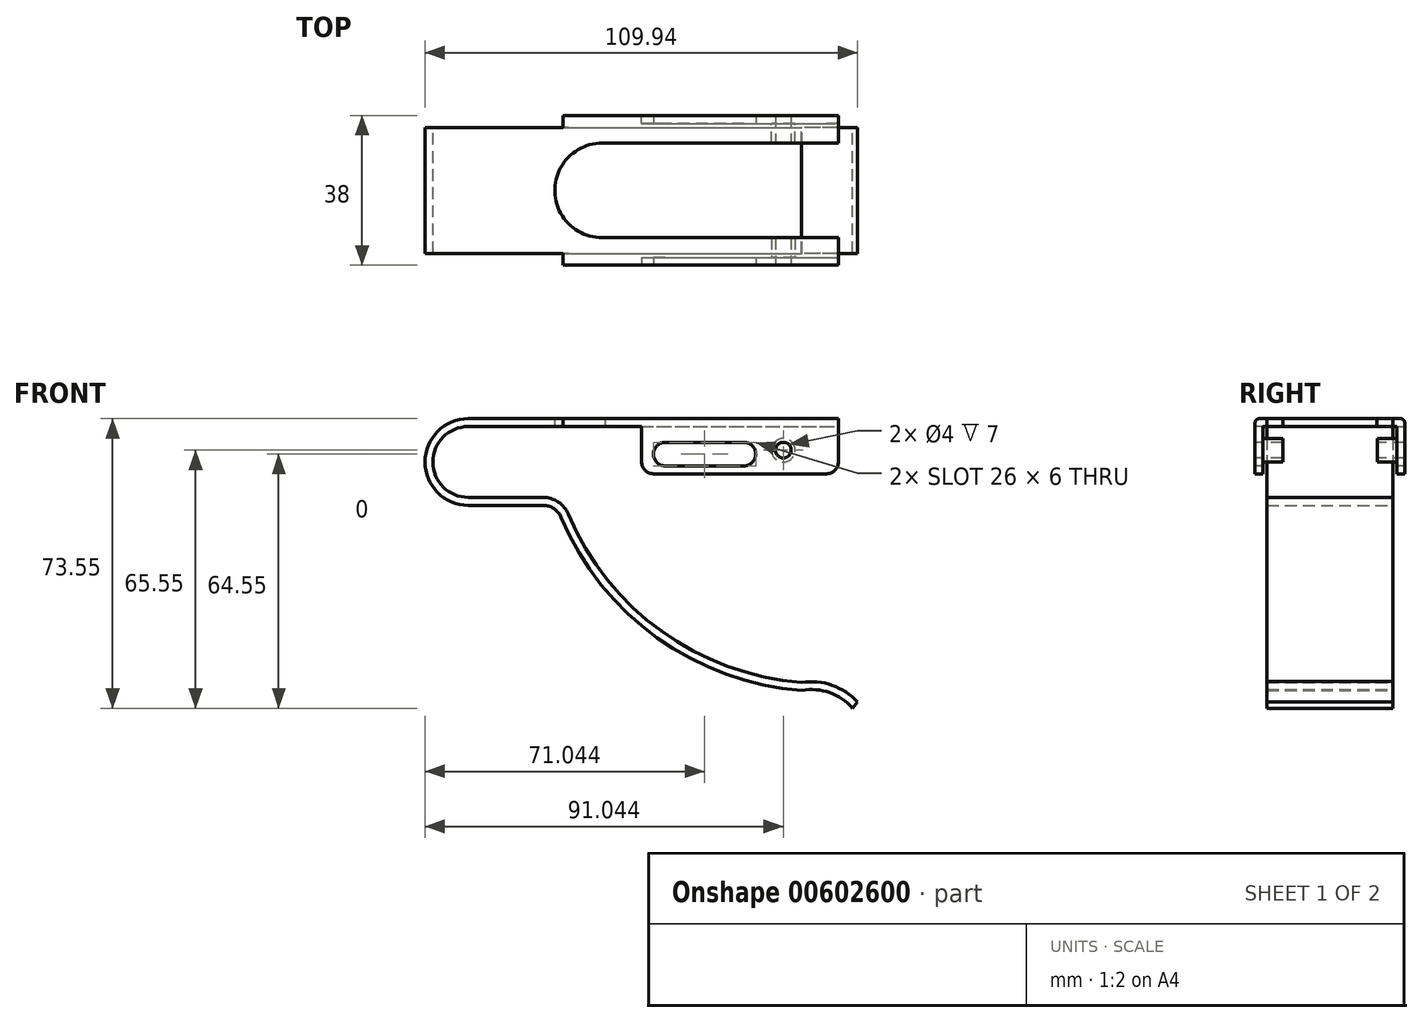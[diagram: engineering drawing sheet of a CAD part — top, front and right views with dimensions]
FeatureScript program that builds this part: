
annotation { "Feature Type Name" : "Feature", "Feature Type Description" : "" }
export const myFeature = defineFeature(function(context is Context, id is Id, definition is map)
    precondition{}
    {
        {
            var Q0;
            Q0=qCreatedBy(makeId("Front.planeOp"),FACE);
            var sketch = newSketch(context, id + "F0", { "sketchPlane" : qUnion([Q0])});
            skArc(sketch, "E0", {"start": v(0, 11) * mm, "mid": v(-11, 0) * mm, "end": v(0, -11) * mm});
            skLineSegment(sketch, "E1", {"start": v(0, 11) * mm, "end": v(94, 11) * mm});
            skLineSegment(sketch, "E2", {"start": v(0, -11) * mm, "end": v(19, -11) * mm});
            skArc(sketch, "E3", {"start": v(23.61, -14.06) * mm, "mid": v(48, -44.68) * mm, "end": v(84.8, -58.01) * mm});
            skArc(sketch, "E4", {"start": v(97.64, -62.55) * mm, "mid": v(91.8, -58.6) * mm, "end": v(84.8, -58.01) * mm});
            skPoint(sketch, "E5.visualSharp", {"position": v(22.4, -11) * mm});
            skArc(sketch, "E5.filletArc", {"start": v(23.61, -14.06) * mm, "mid": v(21.77, -11.84) * mm, "end": v(19, -11) * mm});
            skLineSegment(sketch, "E6.0", {"start": v(0, 9) * mm, "end": v(94, 9) * mm});
            skArc(sketch, "E6.1", {"start": v(0, 9) * mm, "mid": v(-9, 0) * mm, "end": v(0, -9) * mm});
            skArc(sketch, "E6.2", {"start": v(98.94, -61) * mm, "mid": v(92.45, -56.72) * mm, "end": v(84.7, -56) * mm});
            skArc(sketch, "E6.3", {"start": v(25.45, -13.3) * mm, "mid": v(49.07, -42.99) * mm, "end": v(84.7, -56) * mm});
            skArc(sketch, "E6.4", {"start": v(25.45, -13.3) * mm, "mid": v(22.88, -10.17) * mm, "end": v(19, -9) * mm});
            skLineSegment(sketch, "E6.5", {"start": v(0, -9) * mm, "end": v(19, -9) * mm});
            skLineSegment(sketch, "E7", {"start": v(97.64, -62.55) * mm, "end": v(98.94, -61) * mm});
            skLineSegment(sketch, "E8", {"start": v(94, 11) * mm, "end": v(94, 9) * mm});
            skSolve(sketch);
        }
        {
            var Q0;
            Q0 = qSketchRegion(id + "F0", true);
            extrude(context, id + "F1", {"entities" : qUnion([Q0]), "depth" : 16 * mm, "offsetDistance" : 25 * mm});
        }
        {
            var Q0;
            Q0=makeQuery(id+"F1.opExtrude","SWEPT_FACE",FACE,{"disambiguationData":[OSD([sQuery(id+"F0.wireOp",EDGE,"E1")])]});
            var sketch = newSketch(context, id + "F2", { "sketchPlane" : qUnion([Q0])});
            skLineSegment(sketch, "E9.bottom", {"start": v(24.04, -16) * mm, "end": v(94.04, -16) * mm});
            skLineSegment(sketch, "E9.top", {"start": v(24.04, -19) * mm, "end": v(94.04, -19) * mm});
            skLineSegment(sketch, "E9.left", {"start": v(24.04, -16) * mm, "end": v(24.04, -19) * mm});
            skLineSegment(sketch, "E9.right", {"start": v(94.04, -16) * mm, "end": v(94.04, -19) * mm});
            skSolve(sketch);
        }
        {
            var Q0;
            Q0 = qSketchRegion(id + "F2", true);
            extrude(context, id + "F3", {"entities" : qUnion([Q0]), "operationType" : NewBodyOperationType.ADD, "oppositeDirection" : true, "depth" : 2 * mm, "offsetDistance" : 25 * mm});
        }
        {
            var Q0;
            Q0=makeQuery(id+"F3.opExtrude","SWEPT_FACE",FACE,{"disambiguationData":[OSD([sQuery(id+"F2.wireOp",EDGE,"E9.top")])]});
            var sketch = newSketch(context, id + "F4", { "sketchPlane" : qUnion([Q0])});
            skLineSegment(sketch, "E10.bottom", {"start": v(44.04, 11) * mm, "end": v(94.04, 11) * mm});
            skLineSegment(sketch, "E10.top", {"start": v(44.04, -3) * mm, "end": v(94.04, -3) * mm});
            skLineSegment(sketch, "E10.left", {"start": v(44.04, 11) * mm, "end": v(44.04, -3) * mm});
            skLineSegment(sketch, "E10.right", {"start": v(94.04, 11) * mm, "end": v(94.04, -3) * mm});
            skSolve(sketch);
        }
        {
            var Q0;
            Q0 = qSketchRegion(id + "F4", true);
            extrude(context, id + "F5", {"entities" : qUnion([Q0]), "operationType" : NewBodyOperationType.ADD, "oppositeDirection" : true, "depth" : 2 * mm, "offsetDistance" : 25 * mm});
        }
        {
            var Q0;
            Q0=makeQuery(id+"F3.opExtrude","CAP_EDGE",EDGE,{"disambiguationData":[OSD([sQuery(id+"F2.wireOp",EDGE,"E9.top")])],"isStart":true});
            fillet(context, id + "F6", {"entities" : qUnion([Q0]), "radius" : 1 * mm, "tangentPropagation" : true, "allowEdgeOverflow" : false});
        }
        {
            var Q0;
            Q0=makeQuery(id+"F1.opExtrude","SWEPT_BODY",BODY,{"disambiguationData":[OSD([sQuery(id+"F0.wireOp",EDGE,"E0"),sQuery(id+"F0.wireOp",EDGE,"E1"),sQuery(id+"F0.wireOp",EDGE,"E2"),sQuery(id+"F0.wireOp",EDGE,"E3"),sQuery(id+"F0.wireOp",EDGE,"E4"),sQuery(id+"F0.wireOp",EDGE,"E5.filletArc"),sQuery(id+"F0.wireOp",EDGE,"E6.0"),sQuery(id+"F0.wireOp",EDGE,"E6.1"),sQuery(id+"F0.wireOp",EDGE,"E6.2"),sQuery(id+"F0.wireOp",EDGE,"E6.3"),sQuery(id+"F0.wireOp",EDGE,"E6.4"),sQuery(id+"F0.wireOp",EDGE,"E6.5"),sQuery(id+"F0.wireOp",EDGE,"E7"),sQuery(id+"F0.wireOp",EDGE,"E8")])]});
            var Q1;
            Q1=qCreatedBy(makeId("Front.planeOp"),FACE);
            mirror(context, id + "F7", {"operationType" : NewBodyOperationType.ADD, "entities" : qUnion([Q0]), "mirrorPlane" : qUnion([Q1])});
        }
        {
            var Q0;
            {var subQ0=makeQuery(id+"F3.boolean.opBoolean","MERGE",FACE,{"derivedFrom":[makeQuery(id+"F1.opExtrude","SWEPT_FACE",FACE,{"disambiguationData":[OSD([sQuery(id+"F0.wireOp",EDGE,"E1")])]}),makeQuery(id+"F3.opExtrude","CAP_FACE",FACE,{"disambiguationData":[OSD([sQuery(id+"F2.wireOp",EDGE,"E9.bottom"),sQuery(id+"F2.wireOp",EDGE,"E9.top"),sQuery(id+"F2.wireOp",EDGE,"E9.left"),sQuery(id+"F2.wireOp",EDGE,"E9.right")])],"isStart":true})]});Q0=makeQuery(id+"F7.boolean.opBoolean","MERGE",FACE,{"derivedFrom":[subQ0,makeQuery(id+"F7.opPattern","COPY",FACE,{"derivedFrom":subQ0,"instanceName":"1"})]});}
            var sketch = newSketch(context, id + "F8", { "sketchPlane" : qUnion([Q0])});
            skArc(sketch, "E11", {"start": v(34.87, 11.97) * mm, "mid": v(22, 0.4) * mm, "end": v(34.08, -12) * mm});
            skLineSegment(sketch, "E12", {"start": v(34.08, -12) * mm, "end": v(94, -12) * mm});
            skLineSegment(sketch, "E13", {"start": v(33.13, 11.97) * mm, "end": v(94, 11.97) * mm});
            skLineSegment(sketch, "E14", {"start": v(94, 11.97) * mm, "end": v(94, -12) * mm});
            skSolve(sketch);
        }
        {
            var Q0;
            Q0 = qSketchRegion(id + "F8", true);
            extrude(context, id + "F9", {"entities" : qUnion([Q0]), "operationType" : NewBodyOperationType.REMOVE, "oppositeDirection" : true, "depth" : 2 * mm, "offsetDistance" : 25 * mm});
        }
        {
            var Q0;
            Q0=makeQuery(id+"F5.boolean.opBoolean","MERGE",FACE,{"derivedFrom":[makeQuery(id+"F3.opExtrude","SWEPT_FACE",FACE,{"disambiguationData":[OSD([sQuery(id+"F2.wireOp",EDGE,"E9.top")])]}),makeQuery(id+"F5.opExtrude","CAP_FACE",FACE,{"disambiguationData":[OSD([sQuery(id+"F4.wireOp",EDGE,"E10.bottom"),sQuery(id+"F4.wireOp",EDGE,"E10.top"),sQuery(id+"F4.wireOp",EDGE,"E10.left"),sQuery(id+"F4.wireOp",EDGE,"E10.right")])],"isStart":true})]});
            var sketch = newSketch(context, id + "F10", { "sketchPlane" : qUnion([Q0])});
            skLineSegment(sketch, "E15", {"start": v(50.04, 2) * mm, "end": v(70.04, 2) * mm});
            skArc(sketch, "E16.0.startCap", {"start": v(50.04, -1) * mm, "mid": v(47.04, 2) * mm, "end": v(50.04, 5) * mm});
            skArc(sketch, "E16.0.endCap", {"start": v(70.04, 5) * mm, "mid": v(73.04, 2) * mm, "end": v(70.04, -1) * mm});
            skLineSegment(sketch, "E16.0.left", {"start": v(50.04, 5) * mm, "end": v(70.04, 5) * mm});
            skLineSegment(sketch, "E16.0.right", {"start": v(50.04, -1) * mm, "end": v(70.04, -1) * mm});
            skPoint(sketch, "E17", {"position": v(80.04, 3) * mm});
            skSolve(sketch);
        }
        {
            var Q0;
            Q0 = qSketchRegion(id + "F10", true);
            extrude(context, id + "F11", {"entities" : qUnion([Q0]), "operationType" : NewBodyOperationType.REMOVE, "endBound" : BoundingType.THROUGH_ALL, "oppositeDirection" : true, "depth" : 25 * mm, "offsetDistance" : 25 * mm});
        }
        {
            var Q0;
            Q0=sQuery(id+"F10.wireOp",VERTEX,"E17");
            var Q1;
            Q1=makeQuery(id+"F1.opExtrude","SWEPT_BODY",BODY,{"disambiguationData":[OSD([sQuery(id+"F0.wireOp",EDGE,"E0"),sQuery(id+"F0.wireOp",EDGE,"E1"),sQuery(id+"F0.wireOp",EDGE,"E2"),sQuery(id+"F0.wireOp",EDGE,"E3"),sQuery(id+"F0.wireOp",EDGE,"E4"),sQuery(id+"F0.wireOp",EDGE,"E5.filletArc"),sQuery(id+"F0.wireOp",EDGE,"E6.0"),sQuery(id+"F0.wireOp",EDGE,"E6.1"),sQuery(id+"F0.wireOp",EDGE,"E6.2"),sQuery(id+"F0.wireOp",EDGE,"E6.3"),sQuery(id+"F0.wireOp",EDGE,"E6.4"),sQuery(id+"F0.wireOp",EDGE,"E6.5"),sQuery(id+"F0.wireOp",EDGE,"E7"),sQuery(id+"F0.wireOp",EDGE,"E8")])]});
            hole(context, id + "F12", {"style" : HoleStyle.SIMPLE, "endStyle" : HoleEndStyle.THROUGH, "holeDiameter" : 4 * mm, "majorDiameter" : 5 * mm, "isTappedThrough" : true, "tappedDepth" : 12 * mm, "tapClearance" : 3, "locations" : qUnion([Q0]), "scope" : qUnion([Q1])});
        }
        {
            var Q0;
            Q0=makeQuery(id+"F5.opExtrude","CAP_FACE",FACE,{"disambiguationData":[OSD([sQuery(id+"F4.wireOp",EDGE,"E10.bottom"),sQuery(id+"F4.wireOp",EDGE,"E10.top"),sQuery(id+"F4.wireOp",EDGE,"E10.left"),sQuery(id+"F4.wireOp",EDGE,"E10.right")])],"isStart":false});
            var sketch = newSketch(context, id + "F13", { "sketchPlane" : qUnion([Q0])});
            skCircle(sketch, "E18.0", {"center": v(-80.04, 3) * mm, "radius": 2 * mm});
            skCircle(sketch, "E19.0", {"center": v(-80.04, 3) * mm, "radius": 3 * mm});
            skSolve(sketch);
        }
        {
            var Q0;
            Q0 = qSketchRegion(id + "F13", true);
            extrude(context, id + "F14", {"entities" : qUnion([Q0]), "operationType" : NewBodyOperationType.ADD, "depth" : 5 * mm, "offsetDistance" : 25 * mm});
        }
        {
            var Q0;
            Q0=makeQuery(id+"F7.opPattern","COPY",FACE,{"derivedFrom":makeQuery(id+"F5.opExtrude","CAP_FACE",FACE,{"disambiguationData":[OSD([sQuery(id+"F4.wireOp",EDGE,"E10.bottom"),sQuery(id+"F4.wireOp",EDGE,"E10.top"),sQuery(id+"F4.wireOp",EDGE,"E10.left"),sQuery(id+"F4.wireOp",EDGE,"E10.right")])],"isStart":false}),"instanceName":"1"});
            var sketch = newSketch(context, id + "F15", { "sketchPlane" : qUnion([Q0])});
            skCircle(sketch, "E20.0", {"center": v(80.04, 3) * mm, "radius": 2 * mm});
            skCircle(sketch, "E21.0", {"center": v(80.04, 3) * mm, "radius": 3 * mm});
            skSolve(sketch);
        }
        {
            var Q0;
            Q0 = qSketchRegion(id + "F15", true);
            extrude(context, id + "F16", {"entities" : qUnion([Q0]), "operationType" : NewBodyOperationType.ADD, "depth" : 5 * mm, "offsetDistance" : 25 * mm});
        }
        {
            var Q0;
            Q0=makeQuery(id+"F7.opPattern","COPY",EDGE,{"derivedFrom":makeQuery(id+"F5.opExtrude","SWEPT_EDGE",EDGE,{"disambiguationData":[OSD([sQuery(id+"F4.wireOp",EDGE,"E10.top"),sQuery(id+"F4.wireOp",EDGE,"E10.right")])]}),"instanceName":"1"});
            var Q1;
            Q1=makeQuery(id+"F5.opExtrude","SWEPT_EDGE",EDGE,{"disambiguationData":[OSD([sQuery(id+"F4.wireOp",EDGE,"E10.top"),sQuery(id+"F4.wireOp",EDGE,"E10.right")])]});
            var Q2;
            Q2=makeQuery(id+"F5.opExtrude","SWEPT_EDGE",EDGE,{"disambiguationData":[OSD([sQuery(id+"F4.wireOp",EDGE,"E10.top"),sQuery(id+"F4.wireOp",EDGE,"E10.left")])]});
            var Q3;
            Q3=makeQuery(id+"F7.opPattern","COPY",EDGE,{"derivedFrom":makeQuery(id+"F5.opExtrude","SWEPT_EDGE",EDGE,{"disambiguationData":[OSD([sQuery(id+"F4.wireOp",EDGE,"E10.top"),sQuery(id+"F4.wireOp",EDGE,"E10.left")])]}),"instanceName":"1"});
            fillet(context, id + "F17", {"entities" : qUnion([Q0, Q1, Q2, Q3]), "radius" : 3 * mm, "tangentPropagation" : true, "allowEdgeOverflow" : false});
        }
    });
